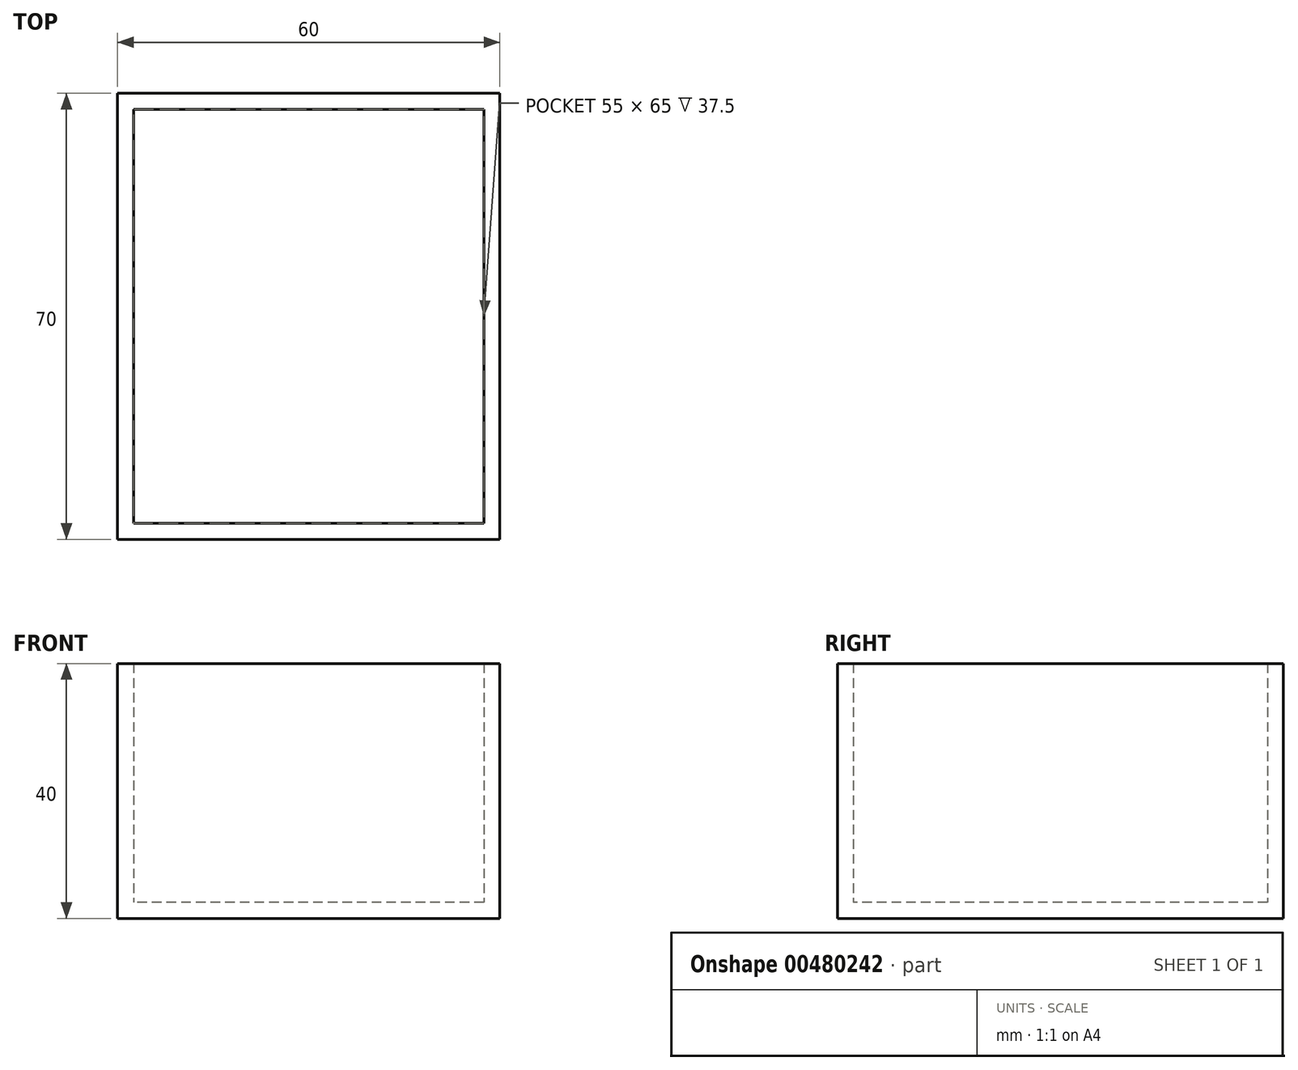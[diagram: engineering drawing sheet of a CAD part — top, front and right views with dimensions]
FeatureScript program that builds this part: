
annotation { "Feature Type Name" : "Feature", "Feature Type Description" : "" }
export const myFeature = defineFeature(function(context is Context, id is Id, definition is map)
    precondition{}
    {
        {
            assignVariable(context, id + "F0", {"name" : "hauteur", "anyValue" : 40});
        }
        {
            var Q0;
            Q0=qCreatedBy(makeId("Top.planeOp"),FACE);
            var sketch = newSketch(context, id + "F1", { "sketchPlane" : qUnion([Q0])});
            skLineSegment(sketch, "E0.bottom", {"start": v(30, 35) * mm, "end": v(-30, 35) * mm});
            skLineSegment(sketch, "E0.top", {"start": v(30, -35) * mm, "end": v(-30, -35) * mm});
            skLineSegment(sketch, "E0.left", {"start": v(30, 35) * mm, "end": v(30, -35) * mm});
            skLineSegment(sketch, "E0.right", {"start": v(-30, 35) * mm, "end": v(-30, -35) * mm});
            skPoint(sketch, "E0.middle", {"position": v(0, 0) * mm});
            skSolve(sketch);
        }
        {
            var Q0;
            Q0 = qSketchRegion(id + "F1", true);
            extrude(context, id + "F2", {"entities" : qUnion([Q0]), "depth" : (getVariable(context, 'hauteur')) * mm});
        }
        {
            var Q0;
            Q0=makeQuery(id+"F2.opExtrude","CAP_FACE",FACE,{"disambiguationData":[OSD([sQuery(id+"F1.wireOp",EDGE,"E0.bottom"),sQuery(id+"F1.wireOp",EDGE,"E0.top"),sQuery(id+"F1.wireOp",EDGE,"E0.left"),sQuery(id+"F1.wireOp",EDGE,"E0.right")])],"isStart":false});
            shell(context, id + "F3", {"entities" : qUnion([Q0]), "thickness" : 2.5 * mm});
        }
    });
